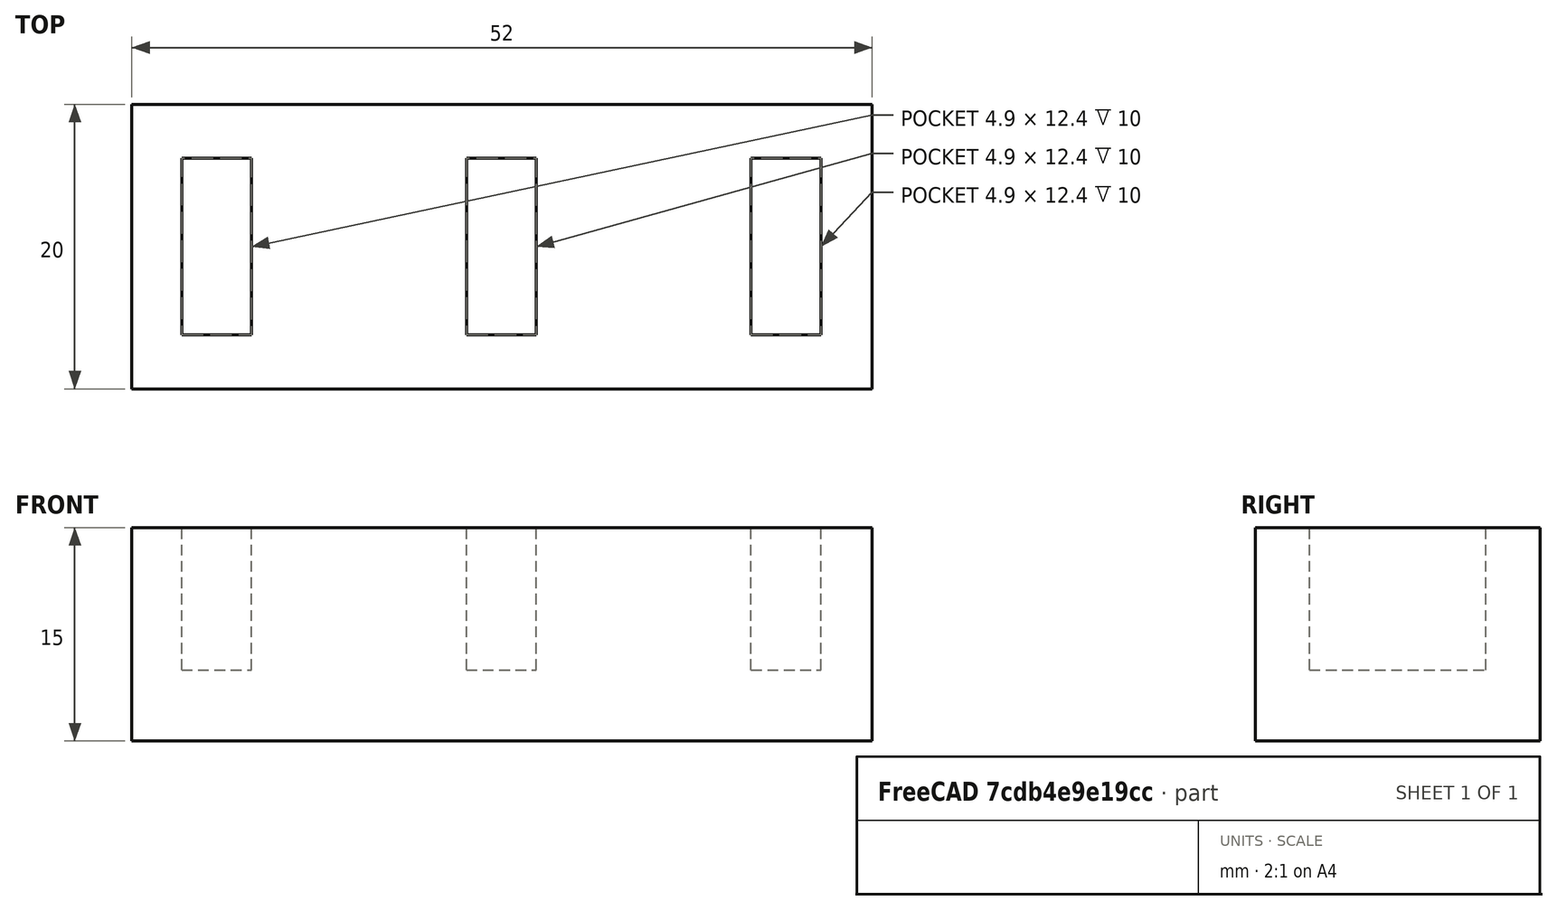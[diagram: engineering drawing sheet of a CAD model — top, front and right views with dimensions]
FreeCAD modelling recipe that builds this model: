
FCSTD DOCUMENT  (FreeCAD 0.20R29177 +233 (Git))
Label: Reto_4_portapen
License: Creative Commons Attribution-ShareAlike
LicenseURL: http://creativecommons.org/licenses/by-sa/4.0/
objects: Part::Box×4, Part::Cut×3
note: 7 computed .brp shape members not serialized (recipe doc carries the construction recipe); baked Part::Feature solids carry a one-line shape summary decoded from their .brp

FEATURE [Part::Box] Box  label="Cubo"
  AttacherType = Attacher::AttachEngine3D
  Height = 15
  Length = 52
  Width = 20
FEATURE [Part::Box] Box001  label="Cubo001"
  AttacherType = Attacher::AttachEngine3D
  Height = 10
  Length = 4.9
  Placement = pos=(3.5,3.8,5) rot=(0,0,1;0rad)
  Width = 12.4
FEATURE [Part::Box] Box002  label="Cubo002"
  AttacherType = Attacher::AttachEngine3D
  Height = 10
  Length = 4.9
  Placement = pos=(23.5,3.8,5) rot=(0,0,1;0rad)
  Width = 12.4
FEATURE [Part::Box] Box003  label="Cubo003"
  AttacherType = Attacher::AttachEngine3D
  Height = 10
  Length = 4.9
  Placement = pos=(43.5,3.8,5) rot=(0,0,1;0rad)
  Width = 12.4
FEATURE [Part::Cut] Cut
  Base = -> Box
  Tool = -> Box001
FEATURE [Part::Cut] Cut001
  Base = -> Cut
  Tool = -> Box002
FEATURE [Part::Cut] Cut002
  Base = -> Cut001
  Tool = -> Box003
